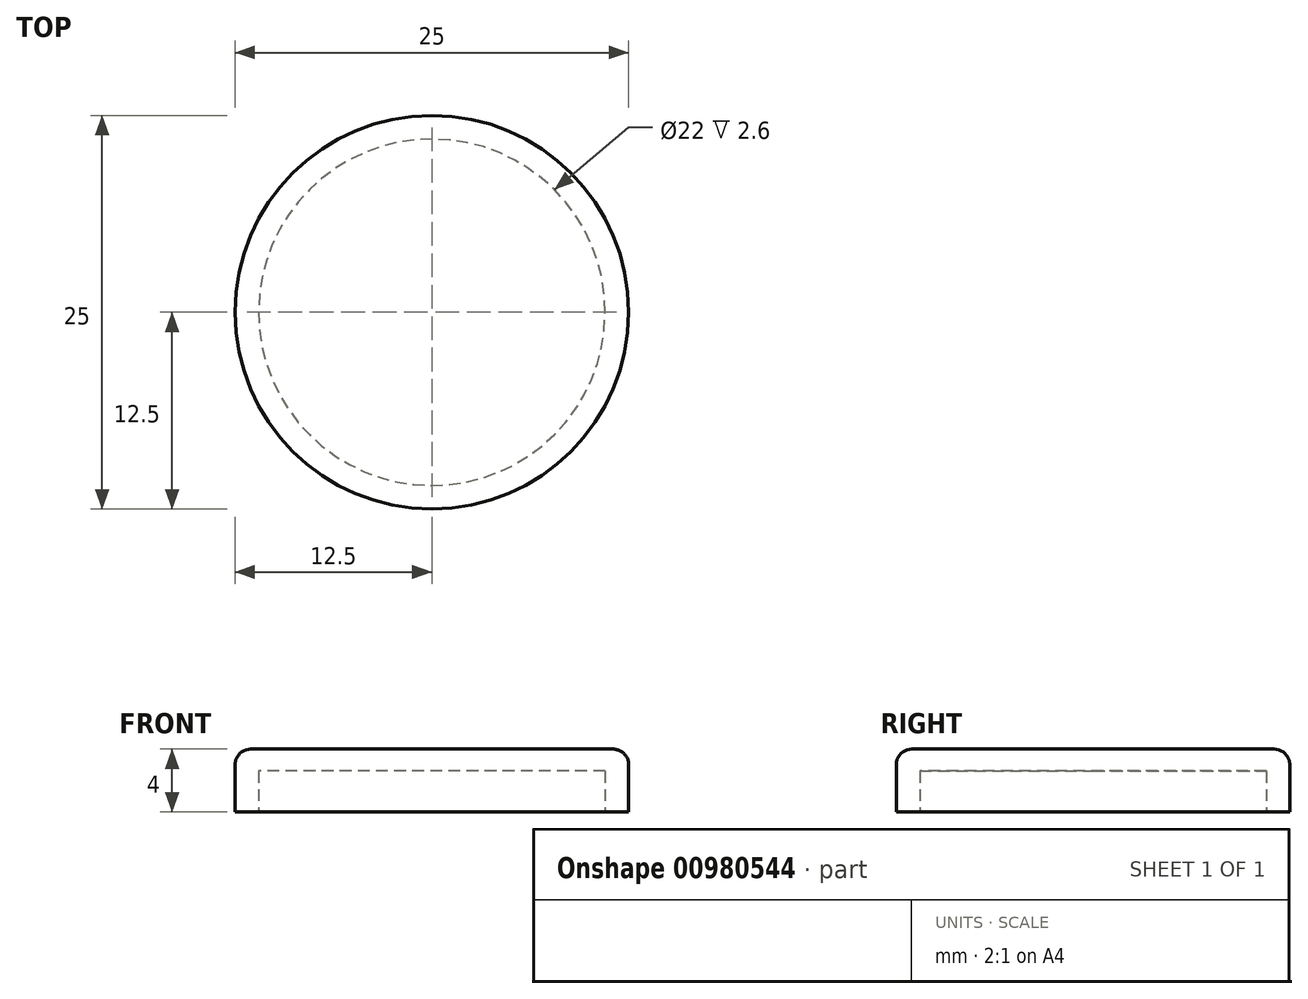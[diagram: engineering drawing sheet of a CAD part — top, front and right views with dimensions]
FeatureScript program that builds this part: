
annotation { "Feature Type Name" : "Feature", "Feature Type Description" : "" }
export const myFeature = defineFeature(function(context is Context, id is Id, definition is map)
    precondition{}
    {
        {
            var Q0;
            Q0=qCreatedBy(makeId("Top.planeOp"),FACE);
            var sketch = newSketch(context, id + "F0", { "sketchPlane" : qUnion([Q0])});
            skCircle(sketch, "E0", {"center": v(0, 0) * mm, "radius": 11 * mm});
            skCircle(sketch, "E1", {"center": v(0, 0) * mm, "radius": 12.5 * mm});
            skSolve(sketch);
        }
        {
            var Q0;
            Q0=makeQuery(id+"F0.imprint","IMPRINT",FACE,{"disambiguationData":[TD([[makeQuery(id+"F0.imprint","IMPRINT",EDGE,{"derivedFrom":sQuery(id+"F0.wireOp",EDGE,"E0")}),-1.0]])]});
            var Q1;
            Q1=makeQuery(id+"F0.imprint","IMPRINT",FACE,{"disambiguationData":[TD([[makeQuery(id+"F0.imprint","IMPRINT",EDGE,{"derivedFrom":sQuery(id+"F0.wireOp",EDGE,"E0")}),1.0]])]});
            extrude(context, id + "F1", {"entities" : qUnion([Q0, Q1]), "depth" : 4 * mm, "offsetDistance" : 25 * mm});
        }
        {
            var Q0;
            Q0=makeQuery(id+"F0.imprint","IMPRINT",FACE,{"disambiguationData":[TD([[makeQuery(id+"F0.imprint","IMPRINT",EDGE,{"derivedFrom":sQuery(id+"F0.wireOp",EDGE,"E0")}),1.0]])]});
            extrude(context, id + "F2", {"entities" : qUnion([Q0]), "operationType" : NewBodyOperationType.REMOVE, "depth" : 2.6 * mm, "offsetDistance" : 25 * mm});
        }
        {
            var Q0;
            Q0=makeQuery(id+"F1.opExtrude","CAP_EDGE",EDGE,{"disambiguationData":[OSD([sQuery(id+"F0.wireOp",EDGE,"E1")])],"isStart":false});
            fillet(context, id + "F3", {"entities" : qUnion([Q0]), "radius" : 1 * mm, "tangentPropagation" : true, "allowEdgeOverflow" : false});
        }
    });
